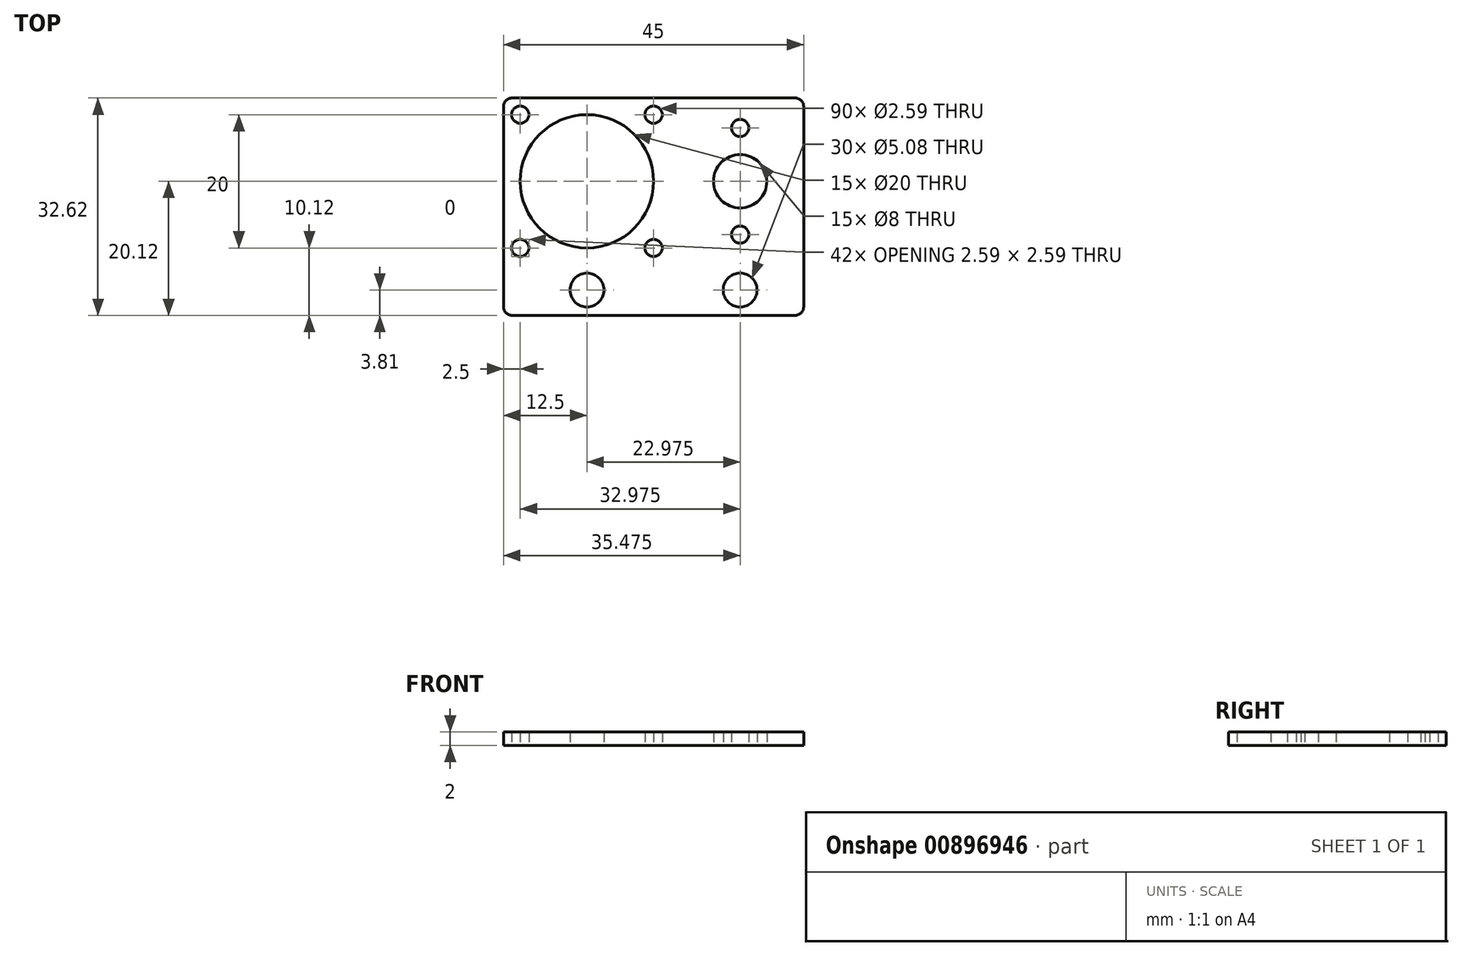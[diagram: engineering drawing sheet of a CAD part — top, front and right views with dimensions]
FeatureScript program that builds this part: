
annotation { "Feature Type Name" : "Feature", "Feature Type Description" : "" }
export const myFeature = defineFeature(function(context is Context, id is Id, definition is map)
    precondition{}
    {
        {
            var Q0;
            Q0=qCreatedBy(makeId("Top.planeOp"),FACE);
            var sketch = newSketch(context, id + "F0", { "sketchPlane" : qUnion([Q0])});
            skLineSegment(sketch, "E0.bottom", {"start": v(22.5, -12.5) * mm, "end": v(-22.5, -12.5) * mm});
            skLineSegment(sketch, "E0.top", {"start": v(22.5, 12.5) * mm, "end": v(-22.5, 12.5) * mm});
            skLineSegment(sketch, "E0.left", {"start": v(22.5, -12.5) * mm, "end": v(22.5, 12.5) * mm});
            skLineSegment(sketch, "E0.right", {"start": v(-22.5, -12.5) * mm, "end": v(-22.5, 12.5) * mm});
            skPoint(sketch, "E0.middle", {"position": v(0, 0) * mm});
            skLineSegment(sketch, "E1", {"start": v(-22.5, 0) * mm, "end": v(-10, 0) * mm});
            skLineSegment(sketch, "E2", {"start": v(22.5, 0) * mm, "end": v(12.97, 0) * mm});
            skLineSegment(sketch, "E3", {"start": v(12.97, 0) * mm, "end": v(12.97, 8) * mm});
            skLineSegment(sketch, "E4", {"start": v(12.97, 0) * mm, "end": v(12.97, -8) * mm});
            skCircle(sketch, "E5", {"center": v(12.97, 0) * mm, "radius": 8 * mm});
            skLineSegment(sketch, "E6.bottom", {"start": v(0, -10) * mm, "end": v(-20, -10) * mm});
            skLineSegment(sketch, "E6.top", {"start": v(0, 10) * mm, "end": v(-20, 10) * mm});
            skLineSegment(sketch, "E6.left", {"start": v(0, -10) * mm, "end": v(0, 10) * mm});
            skLineSegment(sketch, "E6.right", {"start": v(-20, -10) * mm, "end": v(-20, 10) * mm});
            skPoint(sketch, "E6.middle", {"position": v(-10, 0) * mm});
            skCircle(sketch, "E7", {"center": v(12.97, 0) * mm, "radius": 4 * mm});
            skCircle(sketch, "E8", {"center": v(-10, 0) * mm, "radius": 10 * mm});
            skLineSegment(sketch, "E9.bottom", {"start": v(-22.5, -12.5) * mm, "end": v(22.5, -12.5) * mm});
            skLineSegment(sketch, "E9.top", {"start": v(-22.5, -20.12) * mm, "end": v(22.5, -20.12) * mm});
            skLineSegment(sketch, "E9.left", {"start": v(-22.5, -12.5) * mm, "end": v(-22.5, -20.12) * mm});
            skLineSegment(sketch, "E9.right", {"start": v(22.5, -12.5) * mm, "end": v(22.5, -20.12) * mm});
            skLineSegment(sketch, "E10", {"start": v(12.97, 0) * mm, "end": v(12.97, -12.5) * mm});
            skLineSegment(sketch, "E11", {"start": v(12.97, -12.5) * mm, "end": v(12.97, -20.12) * mm});
            skPoint(sketch, "E12", {"position": v(12.97, -16.31) * mm});
            skCircle(sketch, "E13", {"center": v(12.97, -16.31) * mm, "radius": 2.54 * mm});
            skLineSegment(sketch, "E14", {"start": v(12.97, -16.31) * mm, "end": v(-22.5, -16.31) * mm});
            skCircle(sketch, "E15", {"center": v(-10, -16.31) * mm, "radius": 2.54 * mm});
            skSolve(sketch);
        }
        {
            var Q0;
            Q0 = qSketchRegion(id + "F0", true);
            var Q1;
            {var subQ0=sQuery(id+"F0.wireOp",EDGE,"E5");var subQ1=sQuery(id+"F0.wireOp",EDGE,"E3");var subQ2=makeQuery(id+"F0.imprint","INTERSECT",VERTEX,{"derivedFrom":[subQ1,subQ0]});Q1=makeQuery(id+"F0.imprint","IMPRINT",FACE,{"disambiguationData":[TD([[makeQuery(id+"F0.imprint","IMPRINT",EDGE,{"disambiguationData":[TD([[subQ2,1.0]])],"derivedFrom":subQ1}),1.0]])]});}
            var Q2;
            {var subQ0=sQuery(id+"F0.wireOp",EDGE,"E5");var subQ1=sQuery(id+"F0.wireOp",EDGE,"E2");var subQ2=makeQuery(id+"F0.imprint","INTERSECT",VERTEX,{"derivedFrom":[subQ1,subQ0]});Q2=makeQuery(id+"F0.imprint","IMPRINT",FACE,{"disambiguationData":[TD([[makeQuery(id+"F0.imprint","IMPRINT",EDGE,{"disambiguationData":[TD([[subQ2,-1.0]])],"derivedFrom":subQ1}),-1.0]])]});}
            var Q3;
            {var subQ0=sQuery(id+"F0.wireOp",EDGE,"E5");var subQ1=sQuery(id+"F0.wireOp",EDGE,"E2");var subQ2=makeQuery(id+"F0.imprint","INTERSECT",VERTEX,{"derivedFrom":[subQ1,subQ0]});Q3=makeQuery(id+"F0.imprint","IMPRINT",FACE,{"disambiguationData":[TD([[makeQuery(id+"F0.imprint","IMPRINT",EDGE,{"disambiguationData":[TD([[subQ2,-1.0]])],"derivedFrom":subQ1}),1.0]])]});}
            var Q4;
            {var subQ1=sQuery(id+"F0.wireOp",EDGE,"E6.bottom");Q4=makeQuery(id+"F0.imprint","IMPRINT",FACE,{"disambiguationData":[TD([[makeQuery(id+"F0.imprint","IMPRINT",EDGE,{"derivedFrom":subQ1}),-1.0]])]});}
            var Q5;
            {var subQ0=sQuery(id+"F0.wireOp",EDGE,"E6.right");var subQ1=sQuery(id+"F0.wireOp",EDGE,"E6.top");var subQ2=makeQuery(id+"F0.imprint","INTERSECT",VERTEX,{"derivedFrom":[subQ1,subQ0]});Q5=makeQuery(id+"F0.imprint","IMPRINT",FACE,{"disambiguationData":[TD([[makeQuery(id+"F0.imprint","IMPRINT",EDGE,{"disambiguationData":[TD([[subQ2,1.0]])],"derivedFrom":subQ1}),1.0]])]});}
            var Q6;
            {var subQ0=sQuery(id+"F0.wireOp",EDGE,"E6.left");var subQ1=sQuery(id+"F0.wireOp",EDGE,"E6.top");var subQ2=makeQuery(id+"F0.imprint","INTERSECT",VERTEX,{"derivedFrom":[subQ1,subQ0]});Q6=makeQuery(id+"F0.imprint","IMPRINT",FACE,{"disambiguationData":[TD([[makeQuery(id+"F0.imprint","IMPRINT",EDGE,{"disambiguationData":[TD([[subQ2,-1.0]])],"derivedFrom":subQ1}),1.0]])]});}
            extrude(context, id + "F1", {"entities" : qUnion([Q0, Q1, Q2, Q3, Q4, Q5, Q6]), "depth" : 2 * mm, "offsetDistance" : 25.4 * mm});
        }
        {
            var Q0;
            Q0=makeQuery(id+"F1.opExtrude","SWEPT_EDGE",EDGE,{"disambiguationData":[OSD([sQuery(id+"F0.wireOp",EDGE,"E0.top"),sQuery(id+"F0.wireOp",EDGE,"E0.right")])]});
            var Q1;
            Q1=makeQuery(id+"F1.opExtrude","SWEPT_EDGE",EDGE,{"disambiguationData":[OSD([sQuery(id+"F0.wireOp",EDGE,"E0.top"),sQuery(id+"F0.wireOp",EDGE,"E0.left")])]});
            var Q2;
            Q2=makeQuery(id+"F1.opExtrude","SWEPT_EDGE",EDGE,{"disambiguationData":[OSD([sQuery(id+"F0.wireOp",EDGE,"E0.bottom"),sQuery(id+"F0.wireOp",EDGE,"E0.left")])]});
            var Q3;
            Q3=makeQuery(id+"F1.opExtrude","SWEPT_EDGE",EDGE,{"disambiguationData":[OSD([sQuery(id+"F0.wireOp",EDGE,"E0.bottom"),sQuery(id+"F0.wireOp",EDGE,"E0.right")])]});
            var Q4;
            Q4=makeQuery(id+"F1.opExtrude","SWEPT_EDGE",EDGE,{"disambiguationData":[OSD([sQuery(id+"F0.wireOp",EDGE,"E9.top"),sQuery(id+"F0.wireOp",EDGE,"E9.left")])]});
            var Q5;
            Q5=makeQuery(id+"F1.opExtrude","SWEPT_EDGE",EDGE,{"disambiguationData":[OSD([sQuery(id+"F0.wireOp",EDGE,"E9.top"),sQuery(id+"F0.wireOp",EDGE,"E9.right")])]});
            fillet(context, id + "F2", {"entities" : qUnion([Q0, Q1, Q2, Q3, Q4, Q5]), "radius" : 1.27 * mm, "tangentPropagation" : true, "allowEdgeOverflow" : false});
        }
        {
            var Q0;
            Q0=sQuery(id+"F0.wireOp",VERTEX,"E6.top.end");
            var Q1;
            Q1=sQuery(id+"F0.wireOp",VERTEX,"E6.top.start");
            var Q2;
            Q2=sQuery(id+"F0.wireOp",VERTEX,"E6.bottom.start");
            var Q3;
            Q3=sQuery(id+"F0.wireOp",VERTEX,"E6.bottom.end");
            var Q4;
            Q4=sQuery(id+"F0.wireOp",VERTEX,"E3.end");
            var Q5;
            Q5=sQuery(id+"F0.wireOp",VERTEX,"E4.end");
            var Q6;
            Q6=makeQuery(id+"F1.opExtrude","SWEPT_BODY",BODY,{"disambiguationData":[OSD([sQuery(id+"F0.wireOp",EDGE,"E0.bottom"),sQuery(id+"F0.wireOp",EDGE,"E0.top"),sQuery(id+"F0.wireOp",EDGE,"E0.left"),sQuery(id+"F0.wireOp",EDGE,"E0.right"),sQuery(id+"F0.wireOp",EDGE,"E7"),sQuery(id+"F0.wireOp",EDGE,"VDrh0jMb-Uw2y-swJL-ijim-K9hqGZ7CBiJf.bottom"),sQuery(id+"F0.wireOp",EDGE,"VDrh0jMb-Uw2y-swJL-ijim-K9hqGZ7CBiJf.top"),sQuery(id+"F0.wireOp",EDGE,"VDrh0jMb-Uw2y-swJL-ijim-K9hqGZ7CBiJf.left"),sQuery(id+"F0.wireOp",EDGE,"VDrh0jMb-Uw2y-swJL-ijim-K9hqGZ7CBiJf.right")])]});
            hole(context, id + "F3", {"style" : HoleStyle.SIMPLE, "endStyle" : HoleEndStyle.BLIND, "oppositeDirection" : true, "standardTappedOrClearance" : lookupTablePath({ "fit" : "Normal (ASME)", "standard" : "ANSI", "size" : "#2", "type" : "Clearance" }), "standardBlindInLast" : lookupTablePath({ "fit" : "Normal", "standard" : "ANSI", "size" : "#2", "type" : "Clearance" }), "holeDiameter" : 2.6 * mm, "majorDiameter" : 6.35 * mm, "holeDepth" : 3.8 * mm, "isTappedThrough" : true, "tappedDepth" : 12.7 * mm, "tapClearance" : 3, "startFromSketch" : true, "locations" : qUnion([Q0, Q1, Q2, Q3, Q4, Q5]), "scope" : qUnion([Q6])});
        }
    });
